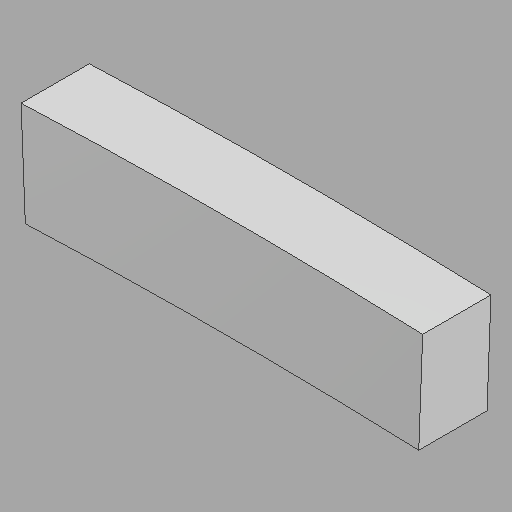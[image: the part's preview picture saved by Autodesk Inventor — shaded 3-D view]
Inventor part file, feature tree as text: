
AUTODESK INVENTOR PART (.ipt)
format: ipt  version: 2022.1 (Build 261234020, 234B)  size: 88,064 bytes
history: imported  units: in
note: dims shown in document units (in); Inventor stores cm internally (conversion verified against a paired STEP export)
features: imported_body x1
ambient origin geometry x8: Origin, YZ Plane, XZ Plane, XY Plane, X Axis, Y Axis, Z Axis, Center Point
bodies: Solid1 (imported_parasolid), Body1 (imported_parasolid)
feature tree (1):
  imported_body  NMx_Import_Brep_tag  [imported B-rep: ~6 faces, bbox_mm=[896.501222, 229.790027, 152.4]]
